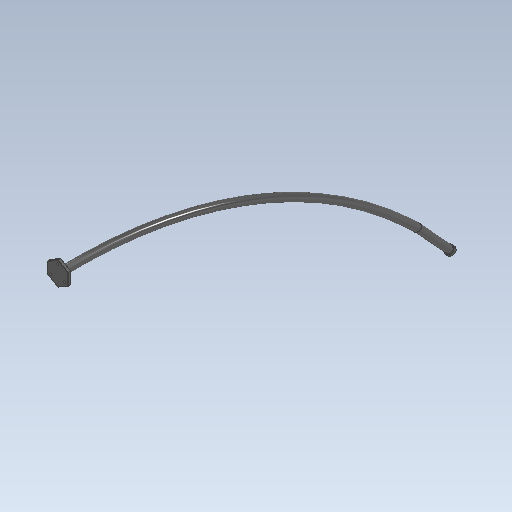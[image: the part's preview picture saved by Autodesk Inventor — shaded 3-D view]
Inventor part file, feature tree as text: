
AUTODESK INVENTOR PART (.ipt)
format: ipt  version: 2021 (Build 250183000, 183)  size: 417,280 bytes
history: native  units: mm
features: sketch x10, extrude x7, fillet x4, sweep x2, plane x2, split x1, hole x1, chamfer x1, projected_geometry x1
ambient origin geometry x8: Origin, YZ Plane, XZ Plane, XY Plane, X Axis, Y Axis, Z Axis, Center Point
bodies: Solid1 (feature_tree), Solid2 (feature_tree), Solid3 (feature_tree)
feature tree (29):
  sketch  "Sketch1"  dims[d0=3300.0mm d1=1650.0mm]
  sweep  "Sweep1"
  sweep  "Sweep2"
  extrude  "Extrusion1"  Depth=23.4mm
  extrude  "Extrusion2"  Depth=1650.0mm
  fillet  "Fillet2"  [1 undecoded]
  plane  "Work Plane1"
  extrude  "Extrusion4"  Depth=3402.0mm
  extrude  "Extrusion5"  Depth=1050.0mm
  extrude  "Extrusion6"  Depth=1701.0mm
  fillet  "Fillet3"  Radius=51.0mm
  extrude  "Extrusion9"  TaperAngle=0.0deg  [1 undecoded]
  extrude  "Extrusion10"  Depth=3.5mm
  fillet  "Fillet6"  Radius=5.0mm
  plane  "Work Plane2"
  split  "Split1"
  fillet  "Fillet7"  [1 undecoded]
  hole  "Hole1"  [1 undecoded]
  chamfer  "Chamfer1"  Angle=120.0deg  [1 undecoded]
  sketch  "Sketch2"  dims[d2=0.0mm d3=25.4mm]
  sketch  "Sketch3"  dims[d4=0.0mm d5=0.0mm d6=23.4mm]
  sketch  "Sketch4"  dims[d7=0.0mm d8=1650.0mm d9=0.0mm d10=0.0mm]
  sketch  "Sketch5"  dims[d11=1752.0mm d12=3402.0mm]
  sketch  "Sketch6"  dims[d13=1701.0mm d14=1050.0mm]
  sketch  "Sketch7"  dims[d15=1701.0mm d16=1701.0mm d17=51.0mm]
  sketch  "Sketch10"  dims[d18=51.0mm d19=0.0mm]
  sketch  "Sketch13"  dims[d20=7.0mm d21=3.5mm d22=5.0mm d23=0.0mm]
  sketch  "Sketch14"  dims[d25=2.0mm d26=-1250.0mm d32=120.0deg d33=120.0deg d34=40.0mm d35=120.0deg d36=120.0deg d37=120.0deg d38=10.0mm d39=0.0mm d40=3300.0mm d41=100.0mm d42=100.0mm d43=0.0mm d44=10.0mm d45=0.0mm d46=1.0mm d53=10.0mm d54=0.0mm d55=7.0mm d56=10.0mm d57=0.0mm d60=3.0mm d61=1.0mm d62=-170.0mm d63=5.0mm d64=12.5mm d65=12.5mm d66=12.5mm d67=8.0mm d68=6.0mm d69=4.0mm d70=2.0mm d71=90.0deg d72=8.0mm d73=20.594885mm d74=1.0mm d75=2.0mm d76=45.0deg]
  projected_geometry  "Projected Loop1"
note: 5 required parameter values undecoded (feature->parameter linkage not recoverable at this tier; creation-order binding heuristic only, values carry confidence <= 0.55)
